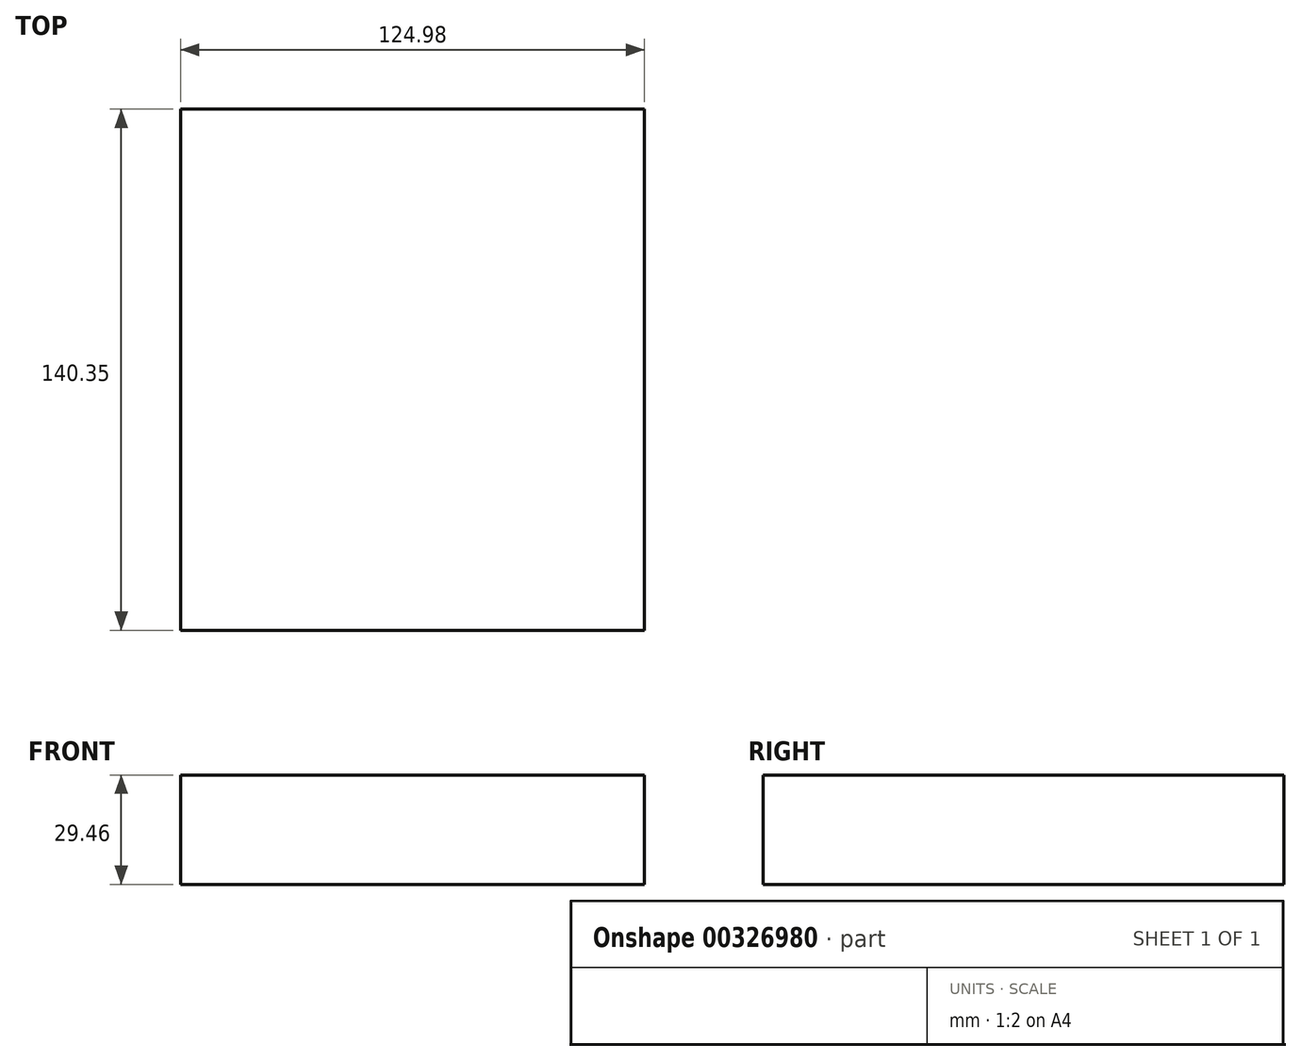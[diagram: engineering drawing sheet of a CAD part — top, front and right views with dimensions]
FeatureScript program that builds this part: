
annotation { "Feature Type Name" : "Feature", "Feature Type Description" : "" }
export const myFeature = defineFeature(function(context is Context, id is Id, definition is map)
    precondition{}
    {
        {
            var Q0;
            Q0=qCreatedBy(makeId("Top.planeOp"),FACE);
            var sketch = newSketch(context, id + "F0", { "sketchPlane" : qUnion([Q0])});
            skLineSegment(sketch, "E0.bottom", {"start": v(-61.05, 64.53) * mm, "end": v(63.93, 64.53) * mm});
            skLineSegment(sketch, "E0.top", {"start": v(-61.05, -75.82) * mm, "end": v(63.93, -75.82) * mm});
            skLineSegment(sketch, "E0.left", {"start": v(-61.05, 64.53) * mm, "end": v(-61.05, -75.82) * mm});
            skLineSegment(sketch, "E0.right", {"start": v(63.93, 64.53) * mm, "end": v(63.93, -75.82) * mm});
            skLineSegment(sketch, "E1", {"start": v(-61.05, -26.61) * mm, "end": v(9.75, -26.61) * mm});
            skLineSegment(sketch, "E2", {"start": v(9.75, -26.61) * mm, "end": v(9.75, 24.05) * mm});
            skLineSegment(sketch, "E3", {"start": v(-61.05, 32.77) * mm, "end": v(9.75, 32.77) * mm});
            skLineSegment(sketch, "E4", {"start": v(30.1, 64.53) * mm, "end": v(30.1, 11.8) * mm});
            skLineSegment(sketch, "E5", {"start": v(9.75, 32.77) * mm, "end": v(18.26, 32.77) * mm});
            skSolve(sketch);
        }
        {
            var Q0;
            {var subQ4=sQuery(id+"F0.wireOp",EDGE,"E0.top");Q0=makeQuery(id+"F0.imprint","IMPRINT",FACE,{"disambiguationData":[TD([[makeQuery(id+"F0.imprint","IMPRINT",EDGE,{"derivedFrom":subQ4}),1.0]])]});}
            extrude(context, id + "F1", {"entities" : qUnion([Q0]), "depth" : 29.46 * mm});
        }
    });
